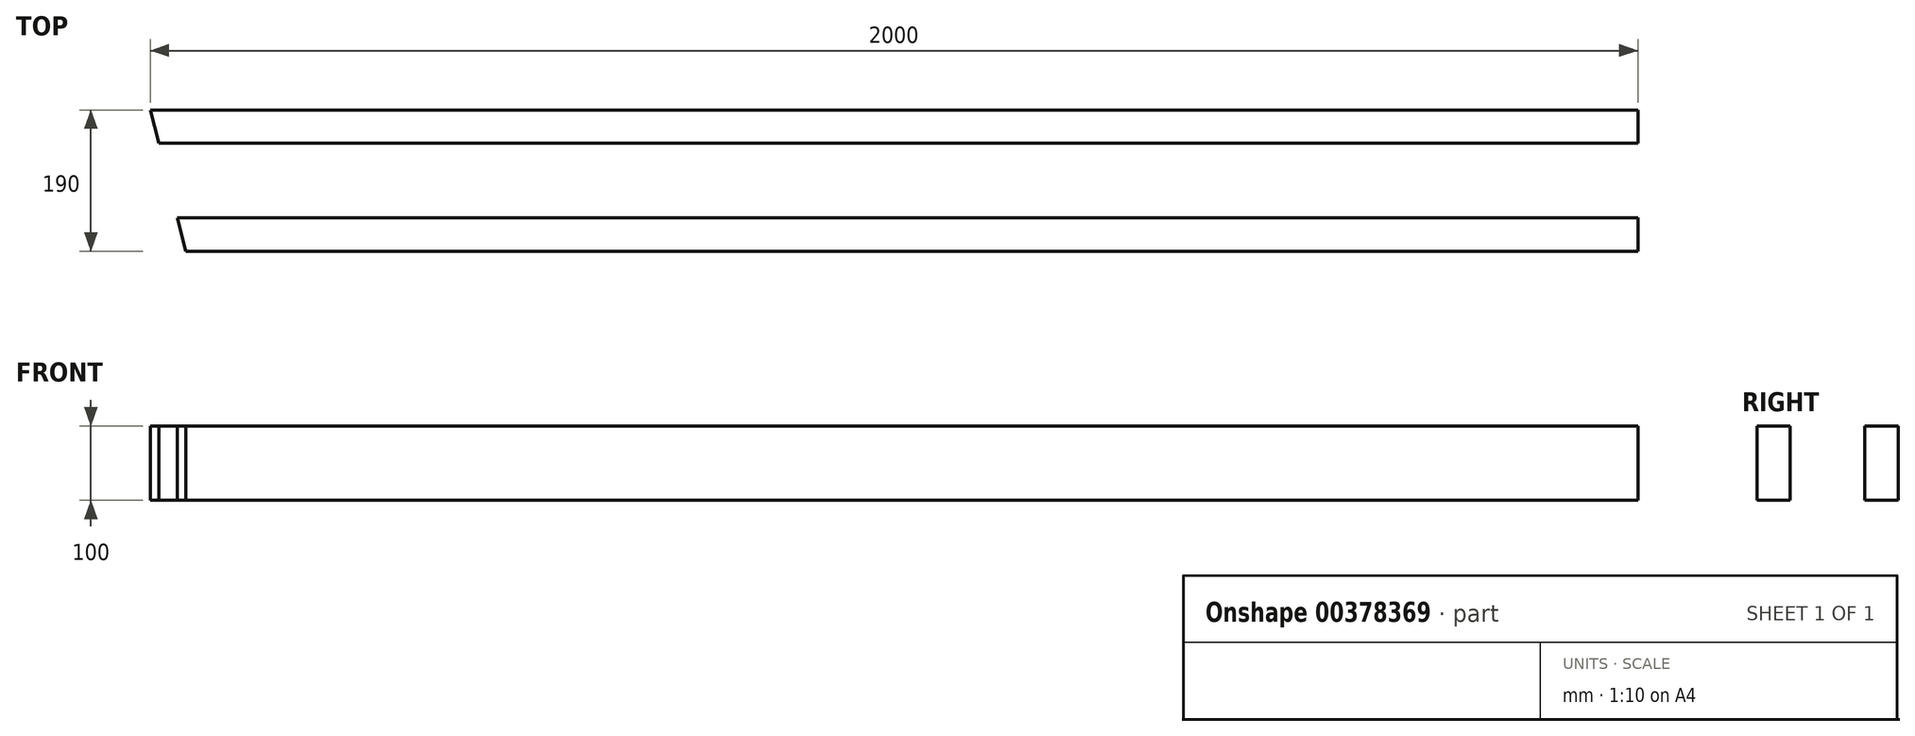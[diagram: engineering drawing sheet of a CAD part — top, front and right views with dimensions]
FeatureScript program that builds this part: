
annotation { "Feature Type Name" : "Feature", "Feature Type Description" : "" }
export const myFeature = defineFeature(function(context is Context, id is Id, definition is map)
    precondition{}
    {
        {
            var Q0;
            Q0=qCreatedBy(makeId("Right.planeOp"),FACE);
            var sketch = newSketch(context, id + "F0", { "sketchPlane" : qUnion([Q0])});
            skLineSegment(sketch, "E0.bottom", {"start": v(-95, 0) * mm, "end": v(-50, 0) * mm});
            skLineSegment(sketch, "E0.top", {"start": v(-95, -100) * mm, "end": v(-50, -100) * mm});
            skLineSegment(sketch, "E0.left", {"start": v(-95, 0) * mm, "end": v(-95, -100) * mm});
            skLineSegment(sketch, "E0.right", {"start": v(-50, 0) * mm, "end": v(-50, -100) * mm});
            skLineSegment(sketch, "E1.bottom", {"start": v(50, 0) * mm, "end": v(95, 0) * mm});
            skLineSegment(sketch, "E1.top", {"start": v(50, -100) * mm, "end": v(95, -100) * mm});
            skLineSegment(sketch, "E1.left", {"start": v(50, 0) * mm, "end": v(50, -100) * mm});
            skLineSegment(sketch, "E1.right", {"start": v(95, 0) * mm, "end": v(95, -100) * mm});
            skSolve(sketch);
        }
        {
            var Q0;
            Q0 = qSketchRegion(id + "F0", true);
            extrude(context, id + "F1", {"entities" : qUnion([Q0]), "depth" : 2000 * mm});
        }
        {
            var Q0;
            Q0=makeQuery(id+"F1.opExtrude","SWEPT_FACE",FACE,{"disambiguationData":[OSD([sQuery(id+"F0.wireOp",EDGE,"E1.bottom")])]});
            var sketch = newSketch(context, id + "F2", { "sketchPlane" : qUnion([Q0])});
            skLineSegment(sketch, "E2", {"start": v(0, 95) * mm, "end": v(47.37, -95) * mm});
            skLineSegment(sketch, "E3", {"start": v(47.37, -95) * mm, "end": v(0, -95) * mm});
            skLineSegment(sketch, "E4", {"start": v(0, -95) * mm, "end": v(0, 95) * mm});
            skSolve(sketch);
        }
        {
            var Q0;
            Q0 = qSketchRegion(id + "F2", true);
            extrude(context, id + "F3", {"entities" : qUnion([Q0]), "operationType" : NewBodyOperationType.REMOVE, "oppositeDirection" : true, "depth" : 100 * mm});
        }
    });
